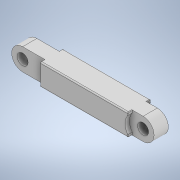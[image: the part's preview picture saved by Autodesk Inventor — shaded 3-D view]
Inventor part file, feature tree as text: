
AUTODESK INVENTOR PART (.ipt)
format: ipt  version: 2021 (Build 250183000, 183)  size: 173,568 bytes
history: native  units: in
note: dims shown in document units (in); Inventor stores cm internally (conversion verified against a paired STEP export)
features: extrude x2, fillet x2, sketch x2
ambient origin geometry x8: Origin, YZ Plane, XZ Plane, XY Plane, X Axis, Y Axis, Z Axis, Center Point
bodies: Solid1 (feature_tree)
feature tree (6):
  extrude  "Extrusion1"  Depth=0.0787in
  extrude  "Extrusion3"  Depth=0.0787in
  fillet  "Fillet3"  Radius=0.1575in
  fillet  "Fillet4"  Radius=0.1024in
  sketch  "Sketch1"  dims[d0=0.1575in d1=0.0787in]
  sketch  "Sketch3"  dims[d2=0.8661in d3=0.0787in d4=0.1575in d5=0.1024in d6=0.0in d16=0.1575in d17=0.1969in d18=0.1654in d19=0.0in d20=0.0079in d21=0.0039in]
